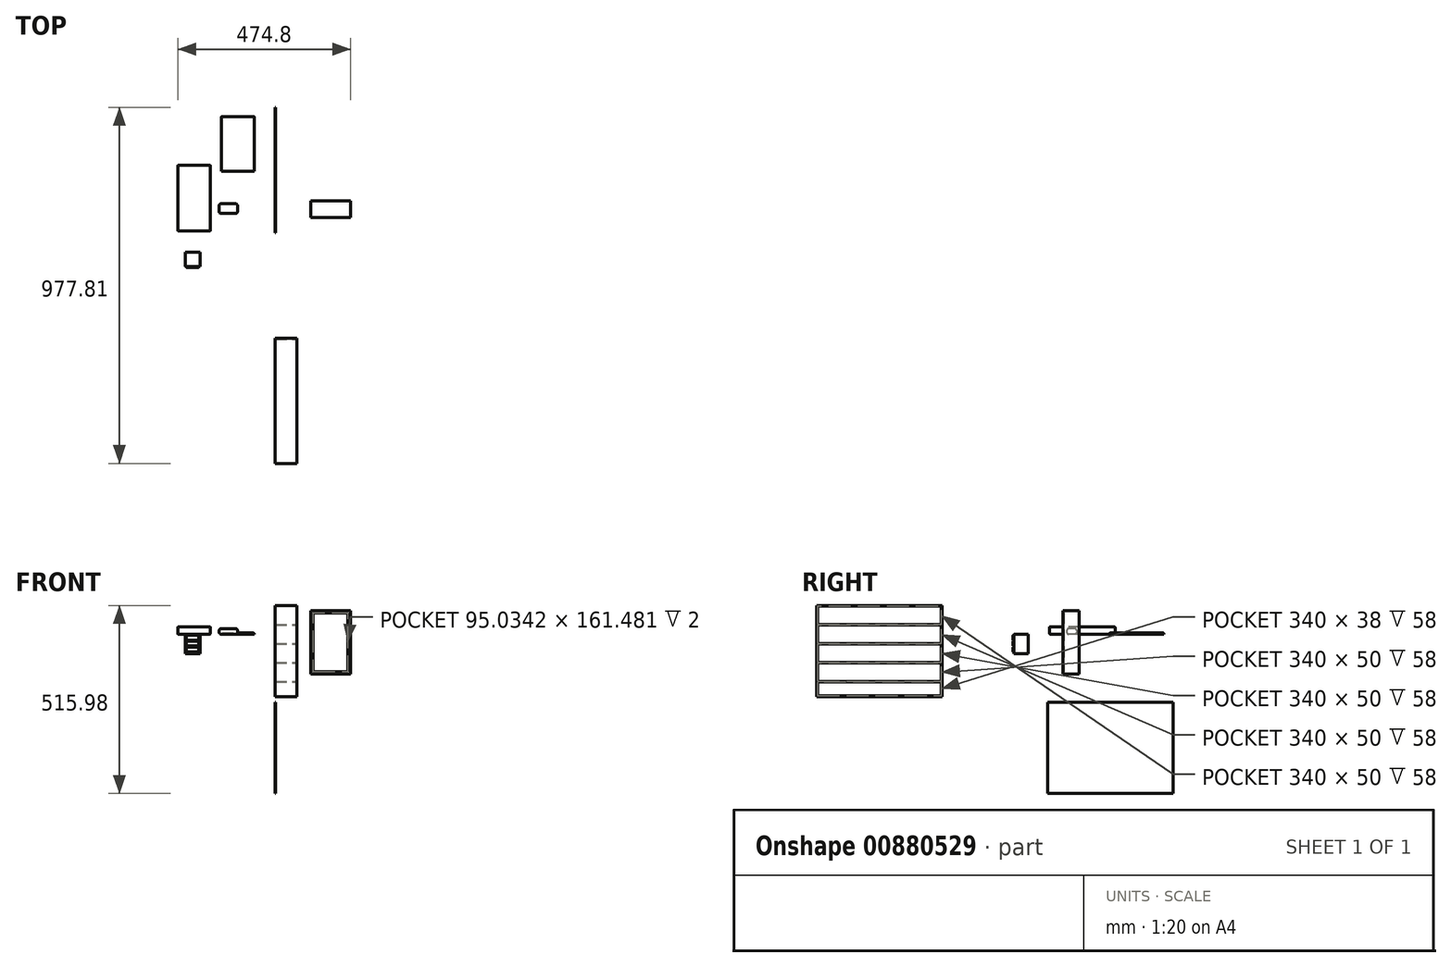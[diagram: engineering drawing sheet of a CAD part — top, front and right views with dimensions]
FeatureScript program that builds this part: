
annotation { "Feature Type Name" : "Feature", "Feature Type Description" : "" }
export const myFeature = defineFeature(function(context is Context, id is Id, definition is map)
    precondition{}
    {
        {
            var Q0;
            Q0=qCreatedBy(makeId("Top.planeOp"),FACE);
            var sketch = newSketch(context, id + "F0", { "sketchPlane" : qUnion([Q0])});
            skLineSegment(sketch, "E0.bottom", {"start": v(-266.7, 98.03) * mm, "end": v(-176.7, 98.03) * mm});
            skLineSegment(sketch, "E0.top", {"start": v(-266.7, -81.97) * mm, "end": v(-176.7, -81.97) * mm});
            skLineSegment(sketch, "E0.left", {"start": v(-266.7, 98.03) * mm, "end": v(-266.7, -81.97) * mm});
            skLineSegment(sketch, "E0.right", {"start": v(-176.7, 98.03) * mm, "end": v(-176.7, -81.97) * mm});
            skSolve(sketch);
        }
        {
            var Q0;
            Q0=makeQuery(id+"F0.imprint","IMPRINT",FACE,{"disambiguationData":[TD([[makeQuery(id+"F0.imprint","IMPRINT",EDGE,{"derivedFrom":sQuery(id+"F0.wireOp",EDGE,"E0.bottom")}),-1.0]])]});
            extrude(context, id + "F1", {"entities" : qUnion([Q0]), "depth" : 20 * mm, "offsetDistance" : 25 * mm});
        }
        {
            var Q0;
            Q0=makeQuery(id+"F1.opExtrude","CAP_FACE",FACE,{"disambiguationData":[OSD([sQuery(id+"F0.wireOp",EDGE,"E0.bottom"),sQuery(id+"F0.wireOp",EDGE,"E0.top"),sQuery(id+"F0.wireOp",EDGE,"E0.left"),sQuery(id+"F0.wireOp",EDGE,"E0.right")])],"isStart":false});
            fillet(context, id + "F2", {"entities" : qUnion([Q0]), "radius" : 2 * mm, "tangentPropagation" : true, "allowEdgeOverflow" : false});
        }
        {
            var Q0;
            Q0=makeQuery(id+"F1.opExtrude","SWEPT_FACE",FACE,{"disambiguationData":[OSD([sQuery(id+"F0.wireOp",EDGE,"E0.top")])]});
            var Q1;
            Q1=makeQuery(id+"F1.opExtrude","SWEPT_FACE",FACE,{"disambiguationData":[OSD([sQuery(id+"F0.wireOp",EDGE,"E0.right")])]});
            var Q2;
            Q2=makeQuery(id+"F1.opExtrude","SWEPT_FACE",FACE,{"disambiguationData":[OSD([sQuery(id+"F0.wireOp",EDGE,"E0.left")])]});
            var Q3;
            Q3=makeQuery(id+"F1.opExtrude","SWEPT_FACE",FACE,{"disambiguationData":[OSD([sQuery(id+"F0.wireOp",EDGE,"E0.bottom")])]});
            var Q4;
            Q4=makeQuery(id+"F1.opExtrude","CAP_FACE",FACE,{"disambiguationData":[OSD([sQuery(id+"F0.wireOp",EDGE,"E0.bottom"),sQuery(id+"F0.wireOp",EDGE,"E0.top"),sQuery(id+"F0.wireOp",EDGE,"E0.left"),sQuery(id+"F0.wireOp",EDGE,"E0.right")])],"isStart":false});
            fillet(context, id + "F3", {"entities" : qUnion([Q0, Q1, Q2, Q3, Q4]), "radius" : 2 * mm, "tangentPropagation" : true, "allowEdgeOverflow" : false});
        }
        {
            var Q0;
            Q0=qCreatedBy(makeId("Top.planeOp"),FACE);
            var sketch = newSketch(context, id + "F4", { "sketchPlane" : qUnion([Q0])});
            skLineSegment(sketch, "E1.bottom", {"start": v(-146.66, 232.2) * mm, "end": v(-56.66, 232.2) * mm});
            skLineSegment(sketch, "E1.top", {"start": v(-146.66, 82.2) * mm, "end": v(-56.66, 82.2) * mm});
            skLineSegment(sketch, "E1.left", {"start": v(-146.66, 232.2) * mm, "end": v(-146.66, 82.2) * mm});
            skLineSegment(sketch, "E1.right", {"start": v(-56.66, 232.2) * mm, "end": v(-56.66, 82.2) * mm});
            skSolve(sketch);
        }
        {
            var Q0;
            Q0=makeQuery(id+"F4.imprint","IMPRINT",FACE,{"disambiguationData":[TD([[makeQuery(id+"F4.imprint","IMPRINT",EDGE,{"derivedFrom":sQuery(id+"F4.wireOp",EDGE,"E1.bottom")}),-1.0]])]});
            extrude(context, id + "F5", {"entities" : qUnion([Q0]), "depth" : 3 * mm, "offsetDistance" : 25 * mm});
        }
        {
            var Q0;
            Q0=makeQuery(id+"F5.opExtrude","CAP_FACE",FACE,{"disambiguationData":[OSD([sQuery(id+"F4.wireOp",EDGE,"E1.bottom"),sQuery(id+"F4.wireOp",EDGE,"E1.top"),sQuery(id+"F4.wireOp",EDGE,"E1.left"),sQuery(id+"F4.wireOp",EDGE,"E1.right")])],"isStart":false});
            fillet(context, id + "F6", {"entities" : qUnion([Q0]), "radius" : 3 * mm, "tangentPropagation" : true, "allowEdgeOverflow" : false});
        }
        {
            var Q0;
            Q0=qCreatedBy(makeId("Top.planeOp"),FACE);
            var sketch = newSketch(context, id + "F7", { "sketchPlane" : qUnion([Q0])});
            skLineSegment(sketch, "E2.bottom", {"start": v(-152.75, -7.34) * mm, "end": v(-102.75, -7.34) * mm});
            skLineSegment(sketch, "E2.top", {"start": v(-152.75, -34.34) * mm, "end": v(-102.75, -34.34) * mm});
            skLineSegment(sketch, "E2.left", {"start": v(-152.75, -7.34) * mm, "end": v(-152.75, -34.34) * mm});
            skLineSegment(sketch, "E2.right", {"start": v(-102.75, -7.34) * mm, "end": v(-102.75, -34.34) * mm});
            skSolve(sketch);
        }
        {
            var Q0;
            Q0=makeQuery(id+"F7.imprint","IMPRINT",FACE,{"disambiguationData":[TD([[makeQuery(id+"F7.imprint","IMPRINT",EDGE,{"derivedFrom":sQuery(id+"F7.wireOp",EDGE,"E2.bottom")}),-1.0]])]});
            extrude(context, id + "F8", {"entities" : qUnion([Q0]), "depth" : 15 * mm, "offsetDistance" : 25 * mm});
        }
        {
            var Q0;
            Q0=makeQuery(id+"F8.opExtrude","CAP_FACE",FACE,{"disambiguationData":[OSD([sQuery(id+"F7.wireOp",EDGE,"E2.bottom"),sQuery(id+"F7.wireOp",EDGE,"E2.top"),sQuery(id+"F7.wireOp",EDGE,"E2.left"),sQuery(id+"F7.wireOp",EDGE,"E2.right")])],"isStart":false});
            var Q1;
            Q1=makeQuery(id+"F8.opExtrude","SWEPT_FACE",FACE,{"disambiguationData":[OSD([sQuery(id+"F7.wireOp",EDGE,"E2.top")])]});
            var Q2;
            Q2=makeQuery(id+"F8.opExtrude","CAP_FACE",FACE,{"disambiguationData":[OSD([sQuery(id+"F7.wireOp",EDGE,"E2.bottom"),sQuery(id+"F7.wireOp",EDGE,"E2.top"),sQuery(id+"F7.wireOp",EDGE,"E2.left"),sQuery(id+"F7.wireOp",EDGE,"E2.right")])],"isStart":true});
            var Q3;
            Q3=makeQuery(id+"F8.opExtrude","SWEPT_FACE",FACE,{"disambiguationData":[OSD([sQuery(id+"F7.wireOp",EDGE,"E2.left")])]});
            var Q4;
            Q4=makeQuery(id+"F8.opExtrude","SWEPT_FACE",FACE,{"disambiguationData":[OSD([sQuery(id+"F7.wireOp",EDGE,"E2.right")])]});
            fillet(context, id + "F9", {"entities" : qUnion([Q0, Q1, Q2, Q3, Q4]), "radius" : 5 * mm, "tangentPropagation" : true, "allowEdgeOverflow" : false});
        }
        {
            var Q0;
            Q0=qCreatedBy(makeId("Front.planeOp"),FACE);
            var sketch = newSketch(context, id + "F10", { "sketchPlane" : qUnion([Q0])});
            skLineSegment(sketch, "E3.bottom", {"start": v(98.1, 64.93) * mm, "end": v(208.1, 64.93) * mm});
            skLineSegment(sketch, "E3.top", {"start": v(98.1, -110.07) * mm, "end": v(208.1, -110.07) * mm});
            skLineSegment(sketch, "E3.left", {"start": v(98.1, 64.93) * mm, "end": v(98.1, -110.07) * mm});
            skLineSegment(sketch, "E3.right", {"start": v(208.1, 64.93) * mm, "end": v(208.1, -110.07) * mm});
            skSolve(sketch);
        }
        {
            var Q0;
            Q0=makeQuery(id+"F10.imprint","IMPRINT",FACE,{"disambiguationData":[TD([[makeQuery(id+"F10.imprint","IMPRINT",EDGE,{"derivedFrom":sQuery(id+"F10.wireOp",EDGE,"E3.bottom")}),-1.0]])]});
            extrude(context, id + "F11", {"entities" : qUnion([Q0]), "depth" : 45 * mm, "offsetDistance" : 25 * mm});
        }
        {
            var Q0;
            Q0=makeQuery(id+"F11.opExtrude","CAP_FACE",FACE,{"disambiguationData":[OSD([sQuery(id+"F10.wireOp",EDGE,"E3.bottom"),sQuery(id+"F10.wireOp",EDGE,"E3.top"),sQuery(id+"F10.wireOp",EDGE,"E3.left"),sQuery(id+"F10.wireOp",EDGE,"E3.right")])],"isStart":false});
            var sketch = newSketch(context, id + "F12", { "sketchPlane" : qUnion([Q0])});
            skLineSegment(sketch, "E4.bottom", {"start": v(104.8, 58.17) * mm, "end": v(199.84, 58.17) * mm});
            skLineSegment(sketch, "E4.top", {"start": v(104.8, -103.31) * mm, "end": v(199.84, -103.31) * mm});
            skLineSegment(sketch, "E4.left", {"start": v(104.8, 58.17) * mm, "end": v(104.8, -103.31) * mm});
            skLineSegment(sketch, "E4.right", {"start": v(199.84, 58.17) * mm, "end": v(199.84, -103.31) * mm});
            skSolve(sketch);
        }
        {
            var Q0;
            Q0=makeQuery(id+"F12.imprint","IMPRINT",FACE,{"disambiguationData":[TD([[makeQuery(id+"F12.imprint","IMPRINT",EDGE,{"derivedFrom":sQuery(id+"F12.wireOp",EDGE,"E4.bottom")}),-1.0]])]});
            extrude(context, id + "F13", {"entities" : qUnion([Q0]), "operationType" : NewBodyOperationType.REMOVE, "oppositeDirection" : true, "depth" : 2 * mm, "offsetDistance" : 25 * mm});
        }
        {
            var Q0;
            Q0=qCreatedBy(makeId("Right.planeOp"),FACE);
            var sketch = newSketch(context, id + "F14", { "sketchPlane" : qUnion([Q0])});
            skLineSegment(sketch, "E5.bottom", {"start": v(-720.57, 78.45) * mm, "end": v(-376.57, 78.45) * mm});
            skLineSegment(sketch, "E5.top", {"start": v(-720.57, -171.55) * mm, "end": v(-376.57, -171.55) * mm});
            skLineSegment(sketch, "E5.left", {"start": v(-720.57, 78.45) * mm, "end": v(-720.57, -171.55) * mm});
            skLineSegment(sketch, "E5.right", {"start": v(-376.57, 78.45) * mm, "end": v(-376.57, -171.55) * mm});
            skSolve(sketch);
        }
        {
            var Q0;
            Q0=makeQuery(id+"F14.imprint","IMPRINT",FACE,{"disambiguationData":[TD([[makeQuery(id+"F14.imprint","IMPRINT",EDGE,{"derivedFrom":sQuery(id+"F14.wireOp",EDGE,"E5.bottom")}),-1.0]])]});
            extrude(context, id + "F15", {"entities" : qUnion([Q0]), "depth" : 60 * mm, "offsetDistance" : 25 * mm});
        }
        {
            var Q0;
            Q0=makeQuery(id+"F15.opExtrude","CAP_FACE",FACE,{"disambiguationData":[OSD([sQuery(id+"F14.wireOp",EDGE,"E5.bottom"),sQuery(id+"F14.wireOp",EDGE,"E5.top"),sQuery(id+"F14.wireOp",EDGE,"E5.left"),sQuery(id+"F14.wireOp",EDGE,"E5.right")])],"isStart":false});
            var sketch = newSketch(context, id + "F16", { "sketchPlane" : qUnion([Q0])});
            skLineSegment(sketch, "E6.bottom", {"start": v(-718.57, 76.45) * mm, "end": v(-378.57, 76.45) * mm});
            skLineSegment(sketch, "E6.top", {"start": v(-718.57, 26.45) * mm, "end": v(-378.57, 26.45) * mm});
            skLineSegment(sketch, "E6.left", {"start": v(-718.57, 76.45) * mm, "end": v(-718.57, 26.45) * mm});
            skLineSegment(sketch, "E6.right", {"start": v(-378.57, 76.45) * mm, "end": v(-378.57, 26.45) * mm});
            skLineSegment(sketch, "E7.bottom", {"start": v(-718.57, 24.45) * mm, "end": v(-378.57, 24.45) * mm});
            skLineSegment(sketch, "E7.top", {"start": v(-718.57, -25.55) * mm, "end": v(-378.57, -25.55) * mm});
            skLineSegment(sketch, "E7.left", {"start": v(-718.57, 24.45) * mm, "end": v(-718.57, -25.55) * mm});
            skLineSegment(sketch, "E7.right", {"start": v(-378.57, 24.45) * mm, "end": v(-378.57, -25.55) * mm});
            skLineSegment(sketch, "E8.bottom", {"start": v(-718.57, -27.55) * mm, "end": v(-378.57, -27.55) * mm});
            skLineSegment(sketch, "E8.top", {"start": v(-718.57, -77.55) * mm, "end": v(-378.57, -77.55) * mm});
            skLineSegment(sketch, "E8.left", {"start": v(-718.57, -27.55) * mm, "end": v(-718.57, -77.55) * mm});
            skLineSegment(sketch, "E8.right", {"start": v(-378.57, -27.55) * mm, "end": v(-378.57, -77.55) * mm});
            skLineSegment(sketch, "E9.bottom", {"start": v(-718.57, -79.55) * mm, "end": v(-378.57, -79.55) * mm});
            skLineSegment(sketch, "E9.top", {"start": v(-718.57, -129.55) * mm, "end": v(-378.57, -129.55) * mm});
            skLineSegment(sketch, "E9.left", {"start": v(-718.57, -79.55) * mm, "end": v(-718.57, -129.55) * mm});
            skLineSegment(sketch, "E9.right", {"start": v(-378.57, -79.55) * mm, "end": v(-378.57, -129.55) * mm});
            skLineSegment(sketch, "E10.bottom", {"start": v(-718.57, -131.55) * mm, "end": v(-378.57, -131.55) * mm});
            skLineSegment(sketch, "E10.top", {"start": v(-718.57, -169.55) * mm, "end": v(-378.57, -169.55) * mm});
            skLineSegment(sketch, "E10.left", {"start": v(-718.57, -131.55) * mm, "end": v(-718.57, -169.55) * mm});
            skLineSegment(sketch, "E10.right", {"start": v(-378.57, -131.55) * mm, "end": v(-378.57, -169.55) * mm});
            skSolve(sketch);
        }
        {
            var Q0;
            Q0=makeQuery(id+"F16.imprint","IMPRINT",FACE,{"disambiguationData":[TD([[makeQuery(id+"F16.imprint","IMPRINT",EDGE,{"derivedFrom":sQuery(id+"F16.wireOp",EDGE,"E6.bottom")}),-1.0]])]});
            var Q1;
            Q1=makeQuery(id+"F16.imprint","IMPRINT",FACE,{"disambiguationData":[TD([[makeQuery(id+"F16.imprint","IMPRINT",EDGE,{"derivedFrom":sQuery(id+"F16.wireOp",EDGE,"E7.bottom")}),-1.0]])]});
            var Q2;
            Q2=makeQuery(id+"F16.imprint","IMPRINT",FACE,{"disambiguationData":[TD([[makeQuery(id+"F16.imprint","IMPRINT",EDGE,{"derivedFrom":sQuery(id+"F16.wireOp",EDGE,"E8.bottom")}),-1.0]])]});
            var Q3;
            Q3=makeQuery(id+"F16.imprint","IMPRINT",FACE,{"disambiguationData":[TD([[makeQuery(id+"F16.imprint","IMPRINT",EDGE,{"derivedFrom":sQuery(id+"F16.wireOp",EDGE,"E9.bottom")}),-1.0]])]});
            var Q4;
            Q4=makeQuery(id+"F16.imprint","IMPRINT",FACE,{"disambiguationData":[TD([[makeQuery(id+"F16.imprint","IMPRINT",EDGE,{"derivedFrom":sQuery(id+"F16.wireOp",EDGE,"E10.bottom")}),-1.0]])]});
            extrude(context, id + "F17", {"entities" : qUnion([Q0, Q1, Q2, Q3, Q4]), "operationType" : NewBodyOperationType.REMOVE, "oppositeDirection" : true, "depth" : 58 * mm, "offsetDistance" : 25 * mm});
        }
        {
            var Q0;
            Q0=qCreatedBy(makeId("Right.planeOp"),FACE);
            var sketch = newSketch(context, id + "F18", { "sketchPlane" : qUnion([Q0])});
            skLineSegment(sketch, "E11.bottom", {"start": v(-86.76, -187.53) * mm, "end": v(257.24, -187.53) * mm});
            skLineSegment(sketch, "E11.top", {"start": v(-86.76, -437.53) * mm, "end": v(257.24, -437.53) * mm});
            skLineSegment(sketch, "E11.left", {"start": v(-86.76, -187.53) * mm, "end": v(-86.76, -437.53) * mm});
            skLineSegment(sketch, "E11.right", {"start": v(257.24, -187.53) * mm, "end": v(257.24, -437.53) * mm});
            skSolve(sketch);
        }
        {
            var Q0;
            Q0=makeQuery(id+"F18.imprint","IMPRINT",FACE,{"disambiguationData":[TD([[makeQuery(id+"F18.imprint","IMPRINT",EDGE,{"derivedFrom":sQuery(id+"F18.wireOp",EDGE,"E11.bottom")}),-1.0]])]});
            extrude(context, id + "F19", {"entities" : qUnion([Q0]), "depth" : 2 * mm, "offsetDistance" : 25 * mm});
        }
        {
            var Q0;
            Q0=qCreatedBy(makeId("Top.planeOp"),FACE);
            var sketch = newSketch(context, id + "F20", { "sketchPlane" : qUnion([Q0])});
            skLineSegment(sketch, "E12.bottom", {"start": v(-245.75, -139.97) * mm, "end": v(-205.75, -139.97) * mm});
            skLineSegment(sketch, "E12.top", {"start": v(-245.75, -179.97) * mm, "end": v(-205.75, -179.97) * mm});
            skLineSegment(sketch, "E12.left", {"start": v(-245.75, -139.97) * mm, "end": v(-245.75, -179.97) * mm});
            skLineSegment(sketch, "E12.right", {"start": v(-205.75, -139.97) * mm, "end": v(-205.75, -179.97) * mm});
            skSolve(sketch);
        }
        {
            var Q0;
            Q0=makeQuery(id+"F20.imprint","IMPRINT",FACE,{"disambiguationData":[TD([[makeQuery(id+"F20.imprint","IMPRINT",EDGE,{"derivedFrom":sQuery(id+"F20.wireOp",EDGE,"E12.bottom")}),-1.0]])]});
            extrude(context, id + "F21", {"entities" : qUnion([Q0]), "oppositeDirection" : true, "depth" : 54 * mm, "offsetDistance" : 25 * mm});
        }
        {
            var Q0;
            Q0=makeQuery(id+"F21.opExtrude","SWEPT_FACE",FACE,{"disambiguationData":[OSD([sQuery(id+"F20.wireOp",EDGE,"E12.top")])]});
            var sketch = newSketch(context, id + "F22", { "sketchPlane" : qUnion([Q0])});
            skLineSegment(sketch, "E13.bottom", {"start": v(-243.5, -3.18) * mm, "end": v(-208.66, -3.18) * mm});
            skLineSegment(sketch, "E13.top", {"start": v(-243.5, -16.34) * mm, "end": v(-208.66, -16.34) * mm});
            skLineSegment(sketch, "E13.left", {"start": v(-243.5, -3.18) * mm, "end": v(-243.5, -16.34) * mm});
            skLineSegment(sketch, "E13.right", {"start": v(-208.66, -3.18) * mm, "end": v(-208.66, -16.34) * mm});
            skLineSegment(sketch, "E14.bottom", {"start": v(-243.5, -19.63) * mm, "end": v(-208.85, -19.63) * mm});
            skLineSegment(sketch, "E14.top", {"start": v(-243.5, -32.79) * mm, "end": v(-208.85, -32.79) * mm});
            skLineSegment(sketch, "E14.left", {"start": v(-243.5, -19.63) * mm, "end": v(-243.5, -32.79) * mm});
            skLineSegment(sketch, "E14.right", {"start": v(-208.85, -19.63) * mm, "end": v(-208.85, -32.79) * mm});
            skLineSegment(sketch, "E15.bottom", {"start": v(-243.69, -36.08) * mm, "end": v(-208.66, -36.08) * mm});
            skLineSegment(sketch, "E15.top", {"start": v(-243.69, -49.05) * mm, "end": v(-208.66, -49.05) * mm});
            skLineSegment(sketch, "E15.left", {"start": v(-243.69, -36.08) * mm, "end": v(-243.69, -49.05) * mm});
            skLineSegment(sketch, "E15.right", {"start": v(-208.66, -36.08) * mm, "end": v(-208.66, -49.05) * mm});
            skSolve(sketch);
        }
        {
            var Q0;
            Q0=makeQuery(id+"F22.imprint","IMPRINT",FACE,{"disambiguationData":[TD([[makeQuery(id+"F22.imprint","IMPRINT",EDGE,{"derivedFrom":sQuery(id+"F22.wireOp",EDGE,"E13.bottom")}),-1.0]])]});
            var Q1;
            Q1=makeQuery(id+"F22.imprint","IMPRINT",FACE,{"disambiguationData":[TD([[makeQuery(id+"F22.imprint","IMPRINT",EDGE,{"derivedFrom":sQuery(id+"F22.wireOp",EDGE,"E14.bottom")}),-1.0]])]});
            var Q2;
            Q2=makeQuery(id+"F22.imprint","IMPRINT",FACE,{"disambiguationData":[TD([[makeQuery(id+"F22.imprint","IMPRINT",EDGE,{"derivedFrom":sQuery(id+"F22.wireOp",EDGE,"E15.bottom")}),-1.0]])]});
            extrude(context, id + "F23", {"entities" : qUnion([Q0, Q1, Q2]), "operationType" : NewBodyOperationType.ADD, "depth" : 2 * mm, "offsetDistance" : 25 * mm});
        }
    });
